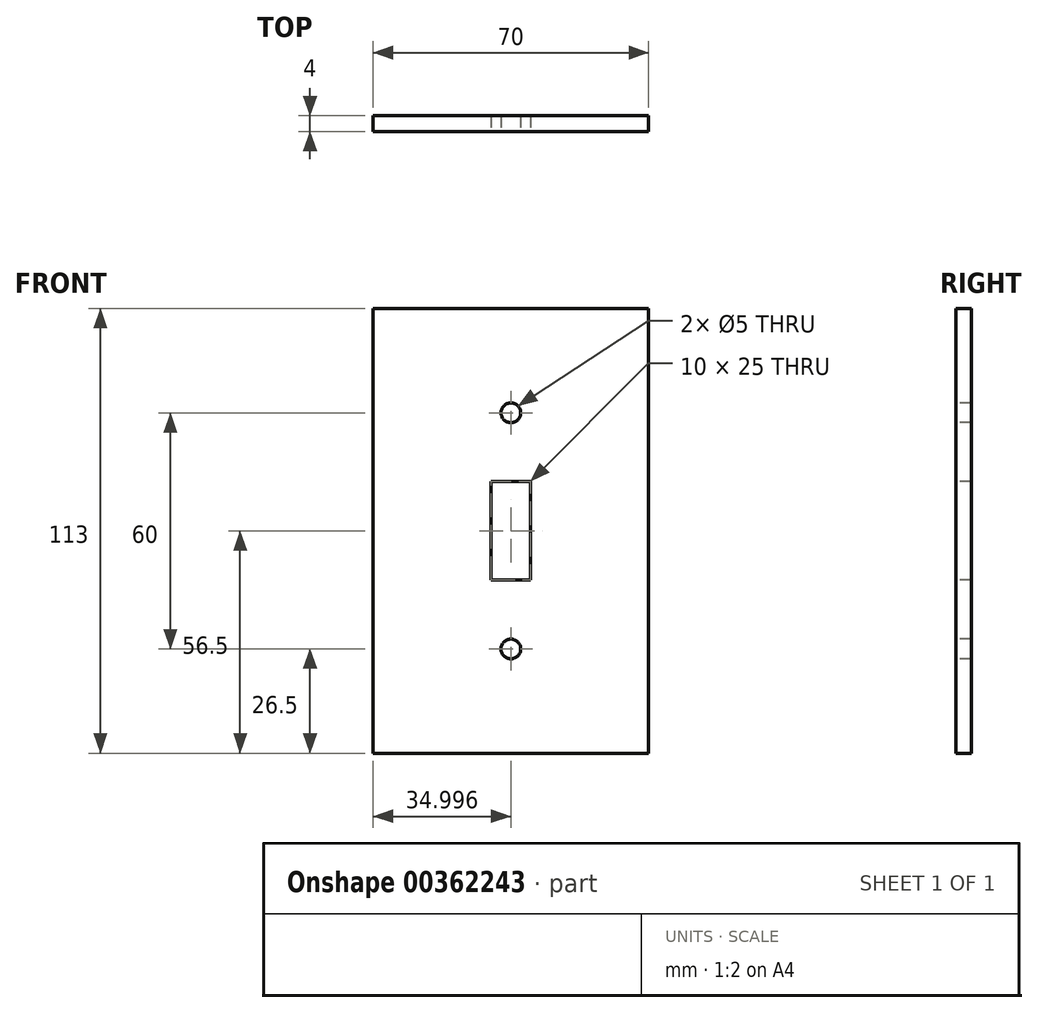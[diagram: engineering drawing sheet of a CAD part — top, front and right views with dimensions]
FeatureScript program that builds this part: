
annotation { "Feature Type Name" : "Feature", "Feature Type Description" : "" }
export const myFeature = defineFeature(function(context is Context, id is Id, definition is map)
    precondition{}
    {
        {
            var Q0;
            Q0=qCreatedBy(makeId("Front.planeOp"),FACE);
            var sketch = newSketch(context, id + "F0", { "sketchPlane" : qUnion([Q0])});
            skLineSegment(sketch, "E0.bottom", {"start": v(-52.11, 55.64) * mm, "end": v(17.89, 55.64) * mm});
            skLineSegment(sketch, "E0.top", {"start": v(-52.11, -57.36) * mm, "end": v(17.89, -57.36) * mm});
            skLineSegment(sketch, "E0.left", {"start": v(-52.11, 55.64) * mm, "end": v(-52.11, -57.36) * mm});
            skLineSegment(sketch, "E0.right", {"start": v(17.89, 55.64) * mm, "end": v(17.89, -57.36) * mm});
            skSolve(sketch);
        }
        {
            var Q0;
            Q0 = qSketchRegion(id + "F0", true);
            extrude(context, id + "F1", {"entities" : qUnion([Q0]), "depth" : 4 * mm});
        }
        {
            var Q0;
            Q0=makeQuery(id+"F1.opExtrude","CAP_FACE",FACE,{"disambiguationData":[OSD([sQuery(id+"F0.wireOp",EDGE,"E0.bottom"),sQuery(id+"F0.wireOp",EDGE,"E0.top"),sQuery(id+"F0.wireOp",EDGE,"E0.left"),sQuery(id+"F0.wireOp",EDGE,"E0.right")])],"isStart":false});
            var sketch = newSketch(context, id + "F2", { "sketchPlane" : qUnion([Q0])});
            skLineSegment(sketch, "E1.bottom", {"start": v(-22.11, 11.64) * mm, "end": v(-12.11, 11.64) * mm});
            skLineSegment(sketch, "E1.top", {"start": v(-22.11, -13.36) * mm, "end": v(-12.11, -13.36) * mm});
            skLineSegment(sketch, "E1.left", {"start": v(-22.11, 11.64) * mm, "end": v(-22.11, -13.36) * mm});
            skLineSegment(sketch, "E1.right", {"start": v(-12.11, 11.64) * mm, "end": v(-12.11, -13.36) * mm});
            skCircle(sketch, "E2", {"center": v(-17.11, 29.14) * mm, "radius": 2.5 * mm});
            skCircle(sketch, "E3", {"center": v(-17.11, -30.86) * mm, "radius": 2.5 * mm});
            skSolve(sketch);
        }
        {
            var Q0;
            Q0 = qSketchRegion(id + "F2", true);
            extrude(context, id + "F3", {"entities" : qUnion([Q0]), "operationType" : NewBodyOperationType.REMOVE, "endBound" : BoundingType.THROUGH_ALL, "oppositeDirection" : true, "depth" : 25 * mm});
        }
    });
